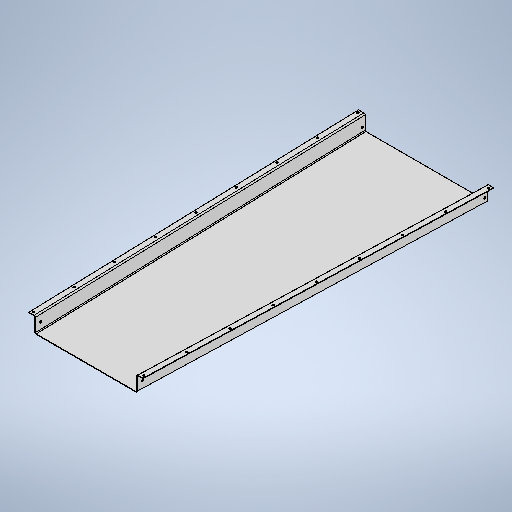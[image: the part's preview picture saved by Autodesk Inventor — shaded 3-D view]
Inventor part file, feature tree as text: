
AUTODESK INVENTOR PART (.ipt)
format: ipt  version: 2025.1 (Build 291241020, 241B)  size: 429,056 bytes
history: native  units: mm
features: sheet_metal_op x7, other x6, sketch x5, projected_geometry x2, extrude x1, pattern_linear x1, mirror x1
ambient origin geometry x8: Origin, YZ Plane, XZ Plane, XY Plane, X Axis, Y Axis, Z Axis, Center Point
bodies: Solid1 (feature_tree)
feature tree (23):
  sheet_metal_op  "Face1"
  other  "A-Side Definition"
  sheet_metal_op  "Flange1"
  sheet_metal_op  "Flange2"
  extrude  "Extrusion1"  Depth=2.0mm
  pattern_linear  "Rectangular Pattern1"  Count1=6 Spacing1=90.0deg
  mirror  "Mirror1"
  sketch  "Sketch1"  dims[d0=460.0mm d2=2.0mm]
  other  "Plate1"
  sketch  "Sketch3"  dims[d12=2.0mm]
  other  "Plate2"
  sheet_metal_op  "Bend1"
  sheet_metal_op  "Corner1"
  sketch  "Sketch4"  dims[d13=1.0mm]
  other  "Plate3"
  sheet_metal_op  "Bend2"
  sheet_metal_op  "Corner2"
  sketch  "Sketch5"  dims[d14=4.0mm]
  projected_geometry  "Projected Loop1"
  sketch  "Sketch6"  dims[d15=2.75mm d16=60.0mm d17=90.0deg d18=2.75mm d19=8.0mm d20=2.0mm d21=2.75mm d23=350.0mm d24=40.0mm d25=470.0mm d26=1300.0mm d27=700.0mm d28=2.0mm d29=1.0mm d30=4.0mm d31=2.75mm d32=25.0mm d33=90.0deg d34=2.75mm d35=8.0mm d36=2.0mm d37=2.75mm d38=8.0mm d39=10.0mm d40=20.0mm d41=0.0mm d42=0.0mm d43=20.0mm d44=7.0mm d45=8.0mm d46=10.0mm d47=2.0mm d48=0.0mm d49=90.0mm d51=160.0mm]
  projected_geometry  "Projected Loop2"
  other  "Cut1"
  other  "Definition1"
